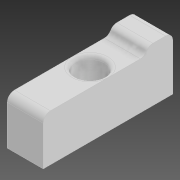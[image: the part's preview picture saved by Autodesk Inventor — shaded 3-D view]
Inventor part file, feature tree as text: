
AUTODESK INVENTOR PART (.ipt)
format: ipt  version: 2020 (Build 240168000, 168)  size: 127,488 bytes
history: native  units: in
note: dims shown in document units (in); Inventor stores cm internally (conversion verified against a paired STEP export)
features: extrude x4, sketch x2, fillet x2
ambient origin geometry x8: Origin, YZ Plane, XZ Plane, XY Plane, X Axis, Y Axis, Z Axis, Center Point
bodies: Solid1 (feature_tree)
feature tree (8):
  sketch  "Sketch1"  dims[d0=0.3937in d1=1.4173in]
  extrude  "Extrusion1"  Depth=1.4173in
  extrude  "Extrusion2"  Depth=0.5118in TaperAngle=0.0deg
  fillet  "Fillet1"  Radius=0.5906in
  sketch  "Sketch2"  dims[d2=0.2756in d3=0.5118in d4=0.0in d5=0.5906in d6=0.0in d7=0.0787in d8=0.315in d9=0.1575in d10=0.5906in d11=0.0in d12=0.3937in d13=0.0in d14=0.0394in]
  extrude  "Extrusion3"  Depth=0.0787in
  extrude  "Extrusion4"  Depth=0.0394in
  fillet  "Fillet2"  Radius=0.1575in
